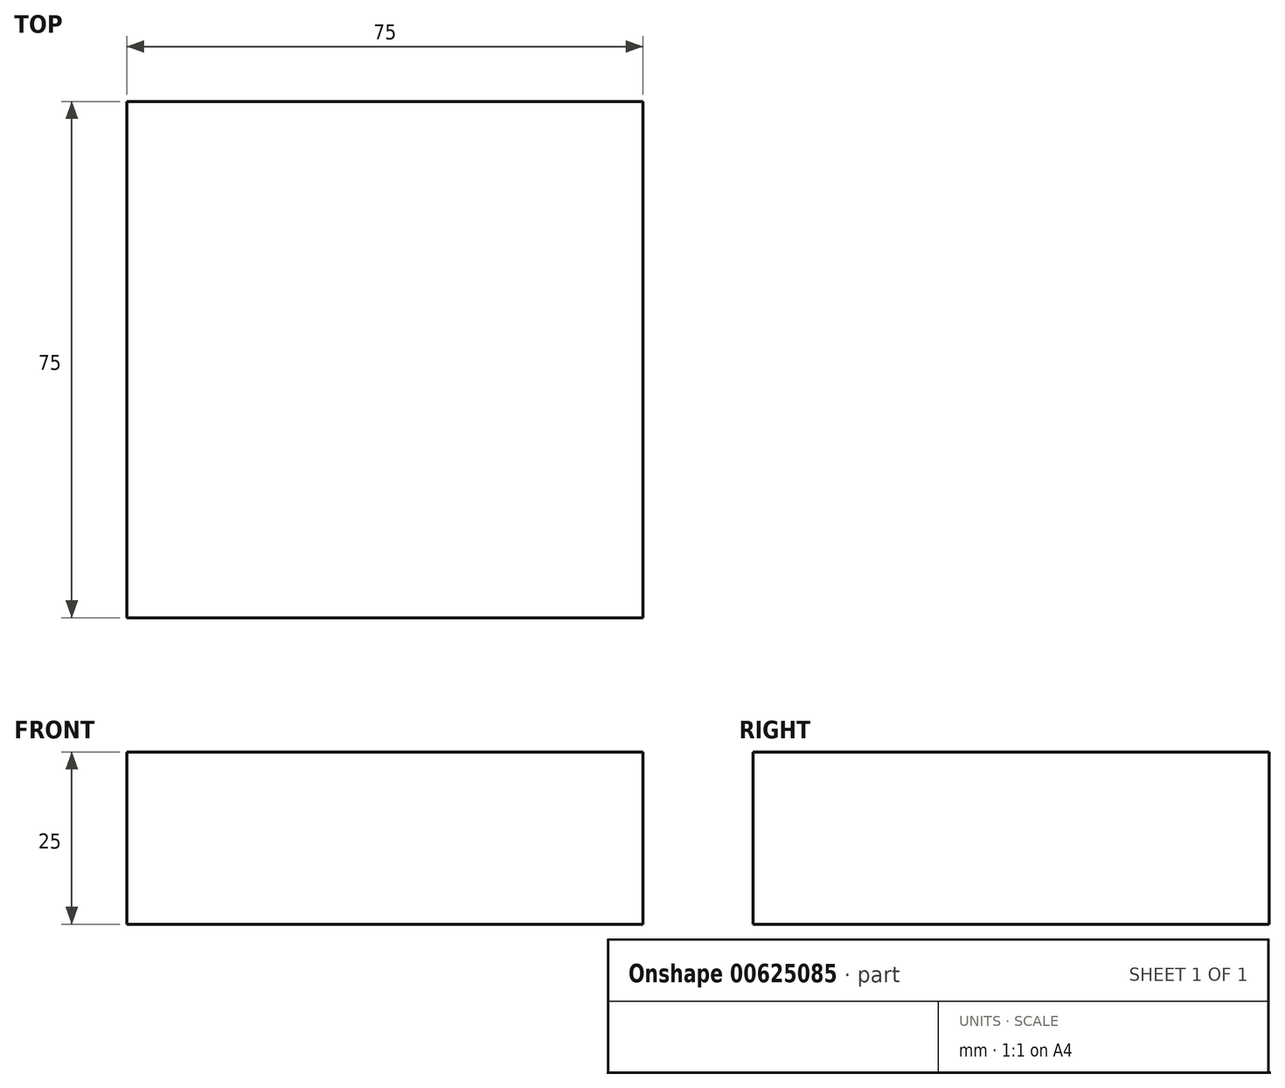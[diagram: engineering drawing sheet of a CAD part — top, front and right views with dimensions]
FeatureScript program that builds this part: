
annotation { "Feature Type Name" : "Feature", "Feature Type Description" : "" }
export const myFeature = defineFeature(function(context is Context, id is Id, definition is map)
    precondition{}
    {
        {
            var Q0;
            Q0=qCreatedBy(makeId("Top.planeOp"),FACE);
            var sketch = newSketch(context, id + "F0", { "sketchPlane" : qUnion([Q0])});
            skLineSegment(sketch, "E0.bottom", {"start": v(-37.5, 37.5) * mm, "end": v(37.5, 37.5) * mm});
            skLineSegment(sketch, "E0.top", {"start": v(-37.5, -37.5) * mm, "end": v(37.5, -37.5) * mm});
            skLineSegment(sketch, "E0.left", {"start": v(-37.5, 37.5) * mm, "end": v(-37.5, -37.5) * mm});
            skLineSegment(sketch, "E0.right", {"start": v(37.5, 37.5) * mm, "end": v(37.5, -37.5) * mm});
            skPoint(sketch, "E0.middle", {"position": v(0, 0) * mm});
            skSolve(sketch);
        }
        {
            var Q0;
            Q0=sQuery(id+"F0.wireOp",EDGE,"E0.bottom");
            var Q1;
            Q1=sQuery(id+"F0.wireOp",EDGE,"E0.left");
            var Q2;
            Q2=sQuery(id+"F0.wireOp",EDGE,"E0.top");
            var Q3;
            Q3=sQuery(id+"F0.wireOp",EDGE,"E0.right");
            extrude(context, id + "F1", {"bodyType" : ToolBodyType.SURFACE, "surfaceEntities" : qUnion([Q0, Q1, Q2, Q3]), "depth" : 25 * mm, "offsetDistance" : 25 * mm});
        }
    });
